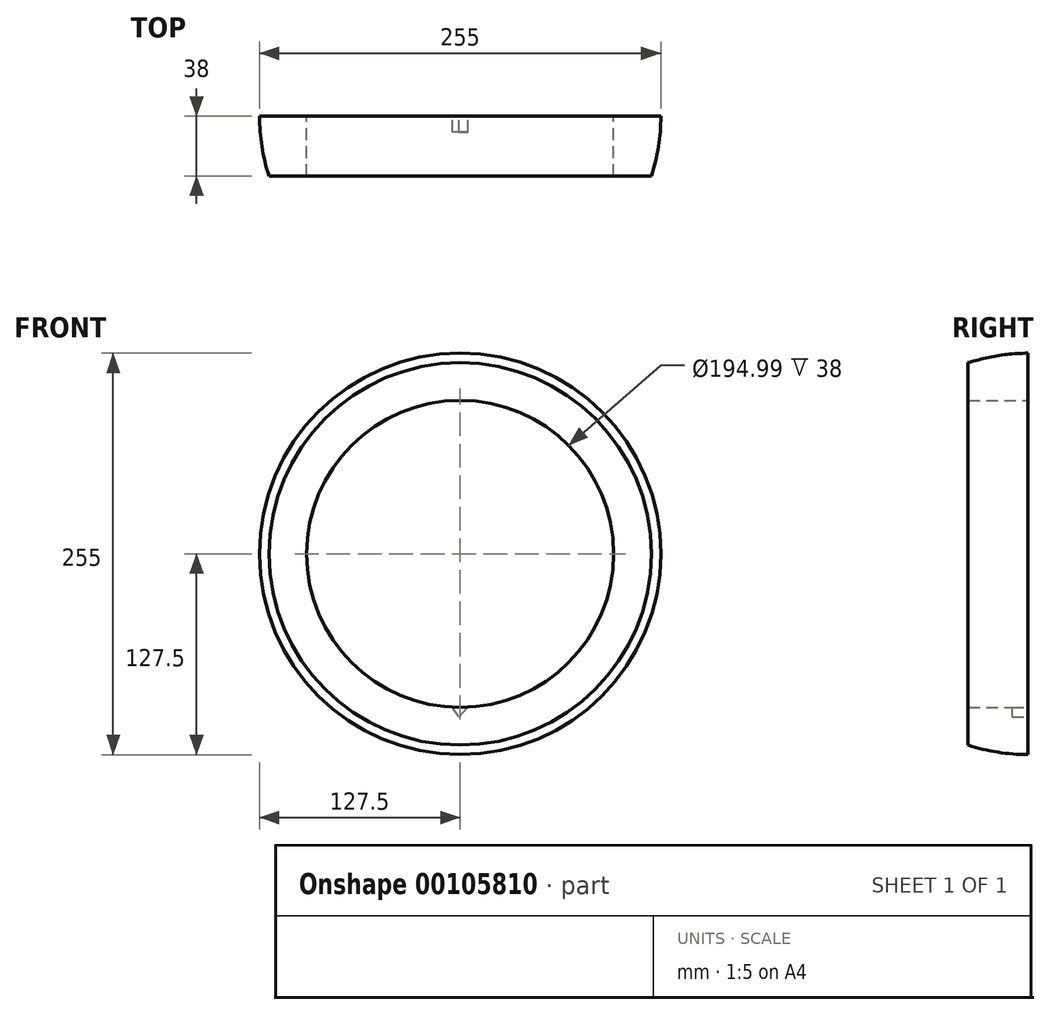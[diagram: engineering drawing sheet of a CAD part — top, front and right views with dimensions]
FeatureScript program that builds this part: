
annotation { "Feature Type Name" : "Feature", "Feature Type Description" : "" }
export const myFeature = defineFeature(function(context is Context, id is Id, definition is map)
    precondition{}
    {
        {
            var Q0;
            Q0=qCreatedBy(makeId("Top.planeOp"),FACE);
            var sketch = newSketch(context, id + "F0", { "sketchPlane" : qUnion([Q0])});
            skLineSegment(sketch, "E0", {"start": v(0, 0) * mm, "end": v(127.5, 0) * mm, "construction": true});
            skCircle(sketch, "E1", {"center": v(0, 0) * mm, "radius": 127.5 * mm, "construction": true});
            skLineSegment(sketch, "E2", {"start": v(0, 74.33) * mm, "end": v(0, -54.8) * mm, "construction": true});
            skArc(sketch, "E3", {"start": v(121.45, -38.82) * mm, "mid": v(125.91, -20.05) * mm, "end": v(127.5, -0.82) * mm});
            skLineSegment(sketch, "E4.bottom", {"start": v(127.5, -0.82) * mm, "end": v(97.5, -0.82) * mm});
            skLineSegment(sketch, "E4.top", {"start": v(127.5, -38.82) * mm, "end": v(97.5, -38.82) * mm});
            skLineSegment(sketch, "E4.left", {"start": v(127.5, -0.82) * mm, "end": v(127.5, -38.82) * mm});
            skLineSegment(sketch, "E4.right", {"start": v(97.5, -0.82) * mm, "end": v(97.5, -38.82) * mm});
            skArc(sketch, "E5", {"start": v(121.45, -38.82) * mm, "mid": v(120.57, -19.67) * mm, "end": v(117.1, -0.82) * mm});
            skSolve(sketch);
        }
        {
            var Q0;
            {var subQ0=sQuery(id+"F0.wireOp",EDGE,"E4.right");Q0=makeQuery(id+"F0.imprint","IMPRINT",FACE,{"disambiguationData":[TD([[makeQuery(id+"F0.imprint","IMPRINT",EDGE,{"derivedFrom":subQ0}),1.0]])]});}
            var Q1;
            {var subQ1=sQuery(id+"F0.wireOp",EDGE,"E3");var subQ3=sQuery(id+"F0.wireOp",EDGE,"E4.top");var subQ4=makeQuery(id+"F0.imprint","INTERSECT",VERTEX,{"derivedFrom":[subQ1,subQ3]});Q1=makeQuery(id+"F0.imprint","IMPRINT",FACE,{"disambiguationData":[TD([[makeQuery(id+"F0.imprint","IMPRINT",EDGE,{"disambiguationData":[TD([[subQ4,-1.0]])],"derivedFrom":subQ3}),-1.0]])]});}
            var Q2;
            {var subQ0=sQuery(id+"F0.wireOp",EDGE,"E5");var subQ1=sQuery(id+"F0.wireOp",EDGE,"E3");var subQ2=makeQuery(id+"F0.imprint","INTERSECT",VERTEX,{"derivedFrom":[subQ1,subQ0]});Q2=makeQuery(id+"F0.imprint","IMPRINT",FACE,{"disambiguationData":[TD([[makeQuery(id+"F0.imprint","IMPRINT",EDGE,{"disambiguationData":[TD([[subQ2,-1.0]])],"derivedFrom":subQ1}),1.0]])]});}
            var Q3;
            Q3=sQuery(id+"F0.wireOp",EDGE,"E2");
            revolve(context, id + "F1", {"entities" : qUnion([Q0, Q1, Q2]), "axis" : qUnion([Q3]), "revolveType" : RevolveType.SYMMETRIC, "angle" : 360 * degree});
        }
        {
            var Q0;
            Q0=makeQuery(id+"F1.opRevolve","SWEPT_FACE",FACE,{"disambiguationData":[OSD([sQuery(id+"F0.wireOp",EDGE,"E4.bottom")])]});
            var sketch = newSketch(context, id + "F2", { "sketchPlane" : qUnion([Q0])});
            skLineSegment(sketch, "E6", {"start": v(0, 0) * mm, "end": v(0, -97.5) * mm});
            skLineSegment(sketch, "E7", {"start": v(7.3, -110.75) * mm, "end": v(-5, -97.37) * mm});
            skLineSegment(sketch, "E8", {"start": v(-5, -97.37) * mm, "end": v(0, -97.5) * mm});
            skLineSegment(sketch, "E9.MirrorCS", {"start": v(-5.45, -112.08) * mm, "end": v(5, -97.2) * mm});
            skLineSegment(sketch, "E10", {"start": v(0, -97.5) * mm, "end": v(5, -97.2) * mm});
            skLineSegment(sketch, "E11", {"start": v(0, 0) * mm, "end": v(92.88, 0) * mm});
            skSolve(sketch);
        }
        {
            var Q0;
            {var subQ0=sQuery(id+"F2.wireOp",EDGE,"E7");Q0=makeQuery(id+"F2.imprint","IMPRINT",FACE,{"disambiguationData":[TD([[makeQuery(id+"F2.imprint","IMPRINT",EDGE,{"derivedFrom":subQ0}),-1.0]])]});}
            extrude(context, id + "F3", {"entities" : qUnion([Q0]), "operationType" : NewBodyOperationType.REMOVE, "oppositeDirection" : true, "depth" : 10 * mm});
        }
    });
